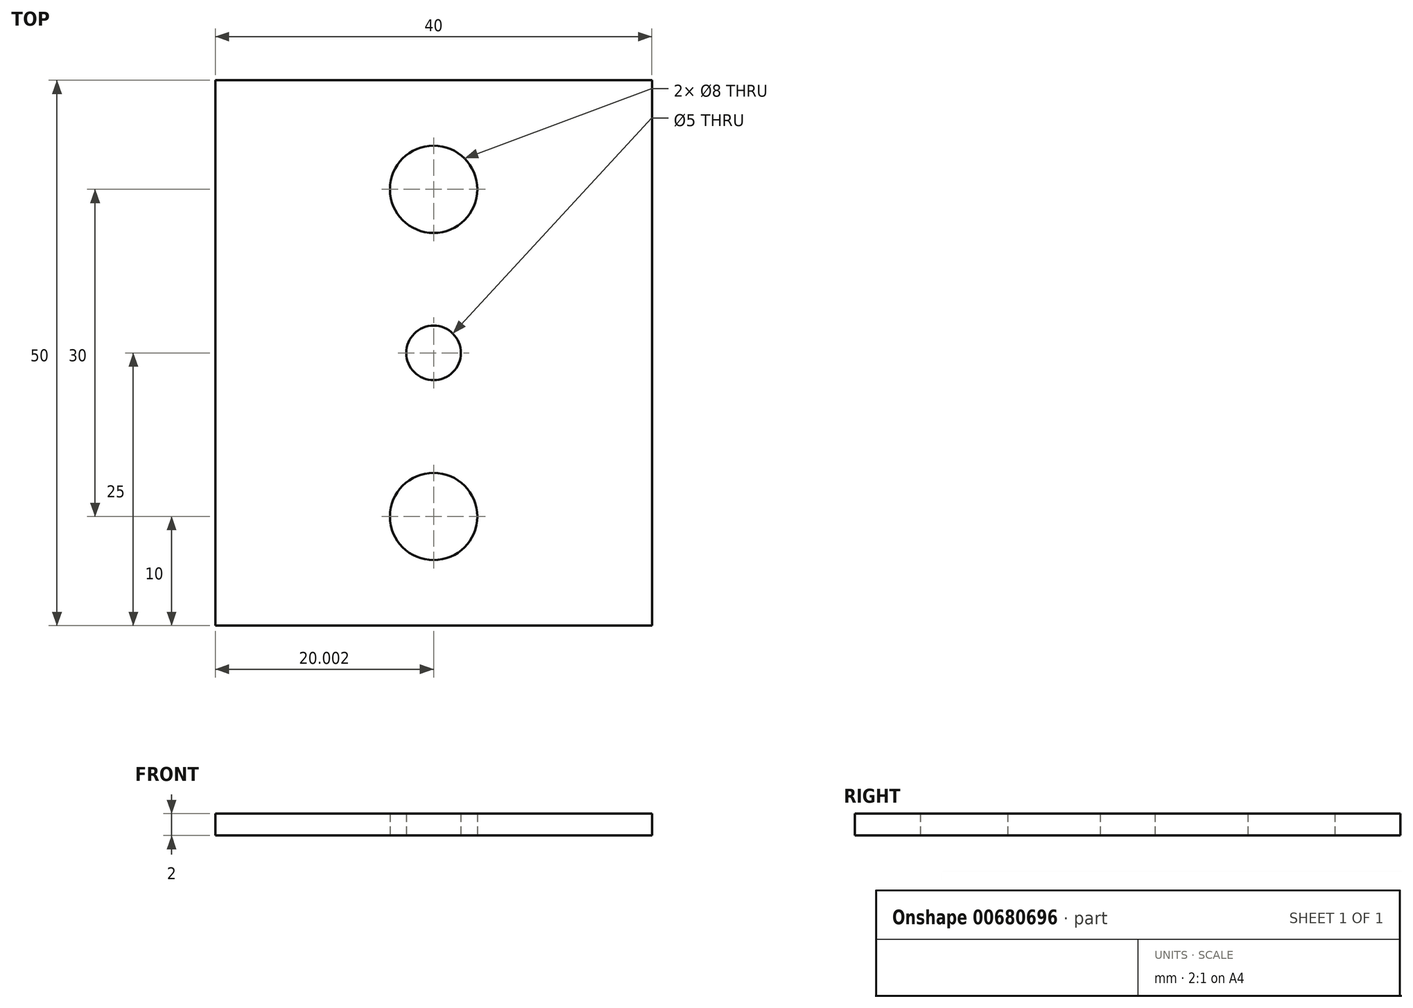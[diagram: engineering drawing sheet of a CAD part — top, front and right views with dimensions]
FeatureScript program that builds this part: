
annotation { "Feature Type Name" : "Feature", "Feature Type Description" : "" }
export const myFeature = defineFeature(function(context is Context, id is Id, definition is map)
    precondition{}
    {
        {
            var Q0;
            Q0=qCreatedBy(makeId("Top.planeOp"),FACE);
            var sketch = newSketch(context, id + "F0", { "sketchPlane" : qUnion([Q0])});
            skLineSegment(sketch, "E0.bottom", {"start": v(22.46, 25) * mm, "end": v(-17.54, 25) * mm});
            skLineSegment(sketch, "E0.top", {"start": v(22.46, -25) * mm, "end": v(-17.54, -25) * mm});
            skLineSegment(sketch, "E0.left", {"start": v(22.46, 25) * mm, "end": v(22.46, -25) * mm});
            skLineSegment(sketch, "E0.right", {"start": v(-17.54, 25) * mm, "end": v(-17.54, -25) * mm});
            skPoint(sketch, "E0.middle", {"position": v(2.46, 0) * mm});
            skCircle(sketch, "E1", {"center": v(2.46, 15) * mm, "radius": 4 * mm});
            skCircle(sketch, "E2", {"center": v(2.46, -15) * mm, "radius": 4 * mm});
            skCircle(sketch, "E3", {"center": v(2.46, 0) * mm, "radius": 2.5 * mm});
            skSolve(sketch);
        }
        {
            var Q0;
            Q0=makeQuery(id+"F0.imprint","IMPRINT",FACE,{"disambiguationData":[TD([[makeQuery(id+"F0.imprint","IMPRINT",EDGE,{"derivedFrom":sQuery(id+"F0.wireOp",EDGE,"E0.bottom")}),1.0]])]});
            extrude(context, id + "F1", {"entities" : qUnion([Q0]), "depth" : 2 * mm, "offsetDistance" : 25 * mm});
        }
    });
